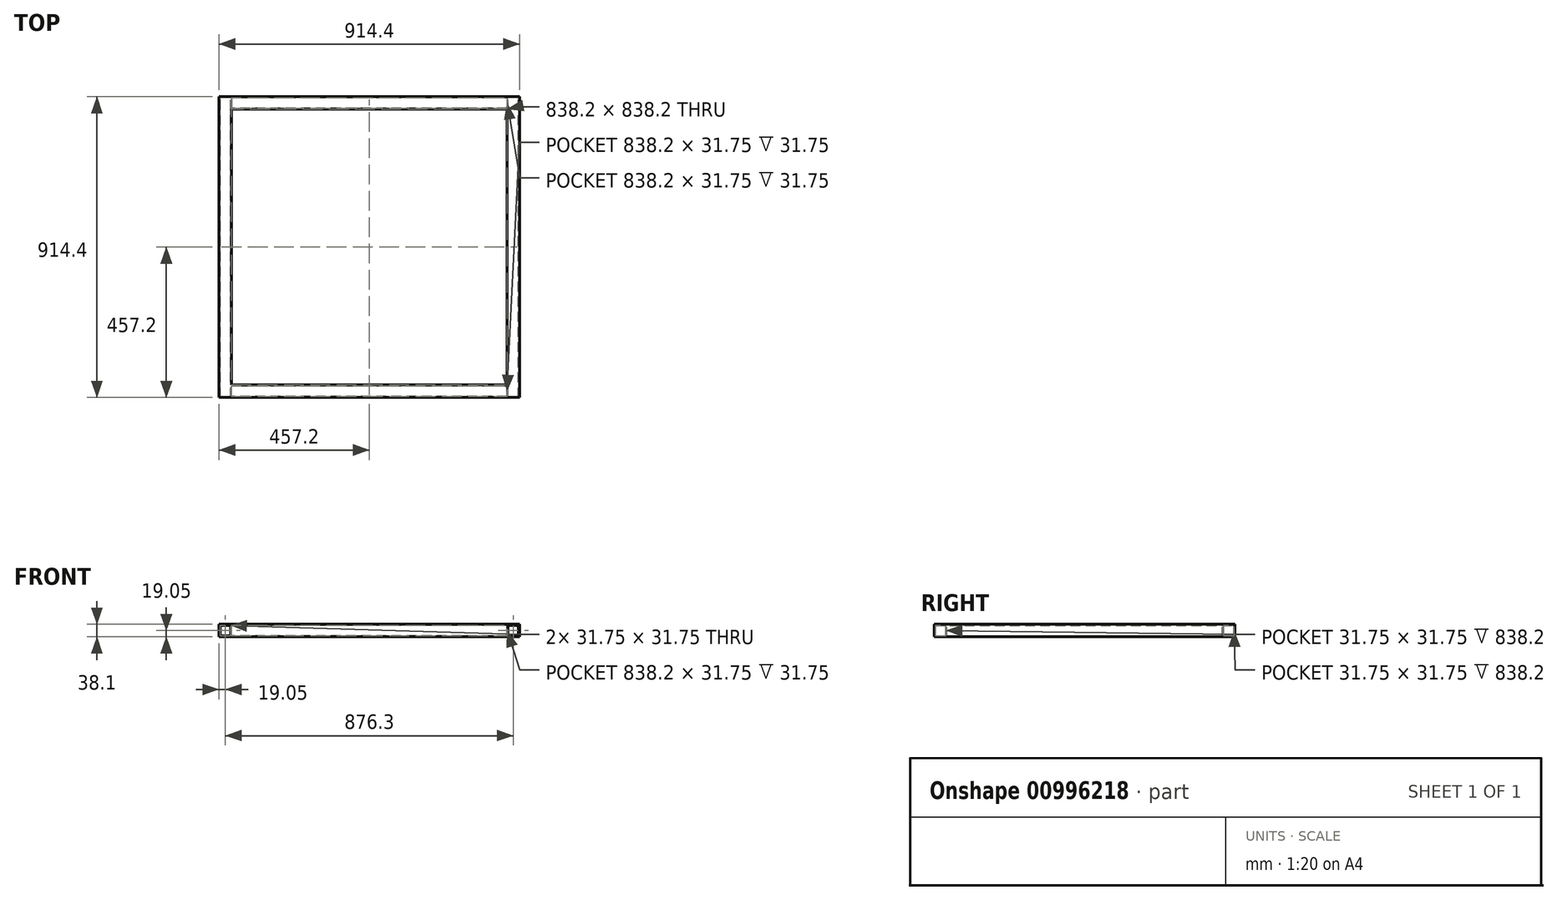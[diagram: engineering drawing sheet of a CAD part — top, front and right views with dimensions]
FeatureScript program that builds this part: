
annotation { "Feature Type Name" : "Feature", "Feature Type Description" : "" }
export const myFeature = defineFeature(function(context is Context, id is Id, definition is map)
    precondition{}
    {
        {
            var Q0;
            Q0=qCreatedBy(makeId("Front.planeOp"),FACE);
            var sketch = newSketch(context, id + "F0", { "sketchPlane" : qUnion([Q0])});
            skLineSegment(sketch, "E0.bottom", {"start": v(0, 0) * mm, "end": v(38.1, 0) * mm});
            skLineSegment(sketch, "E0.top", {"start": v(0, 38.1) * mm, "end": v(38.1, 38.1) * mm});
            skLineSegment(sketch, "E0.left", {"start": v(0, 0) * mm, "end": v(0, 38.1) * mm});
            skLineSegment(sketch, "E0.right", {"start": v(38.1, 0) * mm, "end": v(38.1, 38.1) * mm});
            skLineSegment(sketch, "E1.0", {"start": v(3.17, 3.18) * mm, "end": v(3.17, 34.93) * mm});
            skLineSegment(sketch, "E1.1", {"start": v(3.18, 3.18) * mm, "end": v(34.92, 3.18) * mm});
            skLineSegment(sketch, "E1.2", {"start": v(34.92, 3.18) * mm, "end": v(34.92, 34.93) * mm});
            skLineSegment(sketch, "E1.3", {"start": v(3.17, 34.93) * mm, "end": v(34.92, 34.93) * mm});
            skLineSegment(sketch, "E2.1.0.0", {"start": v(914.4, 0) * mm, "end": v(914.4, 38.1) * mm});
            skLineSegment(sketch, "E2.1.0.1", {"start": v(876.3, 0) * mm, "end": v(914.4, 0) * mm});
            skLineSegment(sketch, "E2.1.0.2", {"start": v(879.48, 3.18) * mm, "end": v(911.23, 3.18) * mm});
            skLineSegment(sketch, "E2.1.0.3", {"start": v(879.48, 3.18) * mm, "end": v(879.48, 34.93) * mm});
            skLineSegment(sketch, "E2.1.0.4", {"start": v(879.48, 34.93) * mm, "end": v(911.23, 34.93) * mm});
            skLineSegment(sketch, "E2.1.0.5", {"start": v(911.23, 3.18) * mm, "end": v(911.23, 34.93) * mm});
            skLineSegment(sketch, "E2.1.0.6", {"start": v(876.3, 0) * mm, "end": v(876.3, 38.1) * mm});
            skLineSegment(sketch, "E2.1.0.7", {"start": v(876.3, 38.1) * mm, "end": v(914.4, 38.1) * mm});
            skLineSegment(sketch, "E2.direction1", {"start": v(0, 0) * mm, "end": v(876.3, 0) * mm, "construction": true});
            skSolve(sketch);
        }
        {
            var Q0;
            Q0=makeQuery(id+"F0.imprint","IMPRINT",FACE,{"disambiguationData":[TD([[makeQuery(id+"F0.imprint","IMPRINT",EDGE,{"derivedFrom":sQuery(id+"F0.wireOp",EDGE,"E0.bottom")}),1.0]])]});
            var Q1;
            Q1=makeQuery(id+"F0.imprint","IMPRINT",FACE,{"disambiguationData":[TD([[makeQuery(id+"F0.imprint","IMPRINT",EDGE,{"derivedFrom":sQuery(id+"F0.wireOp",EDGE,"E2.1.0.0")}),1.0]])]});
            extrude(context, id + "F1", {"entities" : qUnion([Q0, Q1]), "depth" : 914.4 * mm, "offsetDistance" : 25.4 * mm});
        }
        {
            var Q0;
            Q0=makeQuery(id+"F1.opExtrude","SWEPT_FACE",FACE,{"disambiguationData":[OSD([sQuery(id+"F0.wireOp",EDGE,"E0.right")])]});
            var sketch = newSketch(context, id + "F2", { "sketchPlane" : qUnion([Q0])});
            skLineSegment(sketch, "E3.bottom", {"start": v(-914.4, 0) * mm, "end": v(-876.3, 0) * mm});
            skLineSegment(sketch, "E3.top", {"start": v(-914.4, 38.1) * mm, "end": v(-876.3, 38.1) * mm});
            skLineSegment(sketch, "E3.left", {"start": v(-914.4, 0) * mm, "end": v(-914.4, 38.1) * mm});
            skLineSegment(sketch, "E3.right", {"start": v(-876.3, 0) * mm, "end": v(-876.3, 38.1) * mm});
            skLineSegment(sketch, "E4.bottom", {"start": v(0, 0) * mm, "end": v(-38.1, 0) * mm});
            skLineSegment(sketch, "E4.top", {"start": v(0, 38.1) * mm, "end": v(-38.1, 38.1) * mm});
            skLineSegment(sketch, "E4.left", {"start": v(0, 0) * mm, "end": v(0, 38.1) * mm});
            skLineSegment(sketch, "E4.right", {"start": v(-38.1, 0) * mm, "end": v(-38.1, 38.1) * mm});
            skLineSegment(sketch, "E5.0", {"start": v(-911.23, 34.93) * mm, "end": v(-879.48, 34.93) * mm});
            skLineSegment(sketch, "E5.1", {"start": v(-911.23, 3.17) * mm, "end": v(-911.23, 34.93) * mm});
            skLineSegment(sketch, "E5.2", {"start": v(-911.23, 3.17) * mm, "end": v(-879.48, 3.17) * mm});
            skLineSegment(sketch, "E5.3", {"start": v(-879.48, 3.17) * mm, "end": v(-879.48, 34.93) * mm});
            skLineSegment(sketch, "E6.0", {"start": v(-3.18, 3.18) * mm, "end": v(-3.18, 34.93) * mm});
            skLineSegment(sketch, "E6.1", {"start": v(-3.18, 3.18) * mm, "end": v(-34.93, 3.17) * mm});
            skLineSegment(sketch, "E6.2", {"start": v(-34.93, 3.18) * mm, "end": v(-34.93, 34.93) * mm});
            skLineSegment(sketch, "E6.3", {"start": v(-3.18, 34.93) * mm, "end": v(-34.93, 34.93) * mm});
            skSolve(sketch);
        }
        {
            var Q0;
            Q0 = qSketchRegion(id + "F2", true);
            extrude(context, id + "F3", {"entities" : qUnion([Q0]), "operationType" : NewBodyOperationType.ADD, "depth" : 838.2 * mm, "offsetDistance" : 25.4 * mm});
        }
    });
